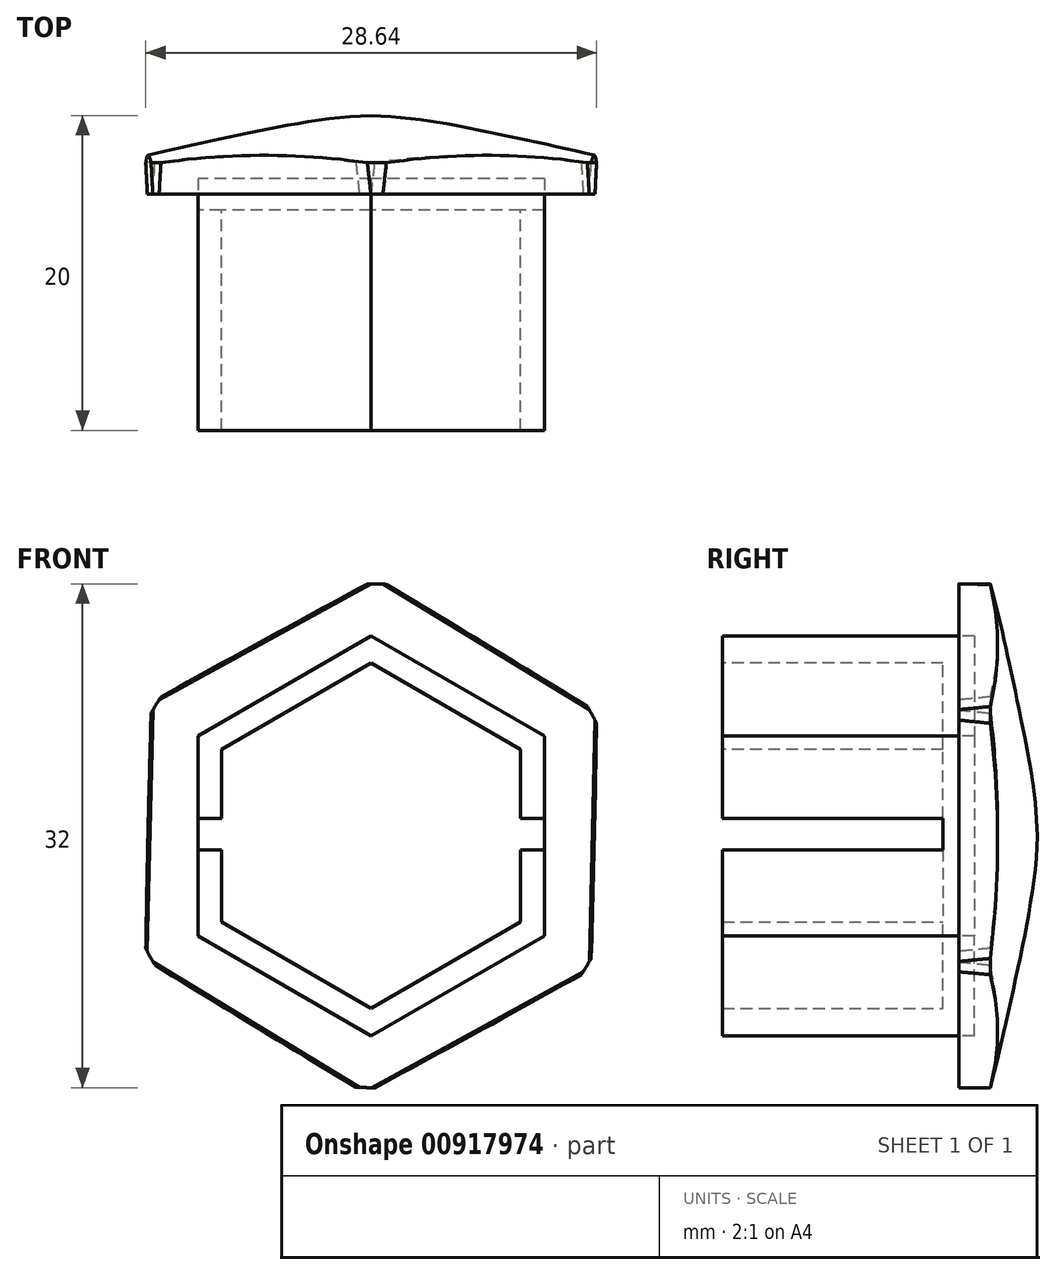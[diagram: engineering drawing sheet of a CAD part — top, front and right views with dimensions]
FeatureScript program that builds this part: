
annotation { "Feature Type Name" : "Feature", "Feature Type Description" : "" }
export const myFeature = defineFeature(function(context is Context, id is Id, definition is map)
    precondition{}
    {
        {
            var Q0;
            Q0=qCreatedBy(makeId("Front.planeOp"),FACE);
            var sketch = newSketch(context, id + "F0", { "sketchPlane" : qUnion([Q0])});
            skCircle(sketch, "E0.cCircle", {"center": v(0, 0) * mm, "radius": 12.7 * mm, "construction": true});
            skLineSegment(sketch, "E0.0", {"start": v(0, -12.7) * mm, "end": v(-11, -6.35) * mm});
            skLineSegment(sketch, "E0.1", {"start": v(-11, -6.35) * mm, "end": v(-11, 6.35) * mm});
            skLineSegment(sketch, "E0.2", {"start": v(-11, 6.35) * mm, "end": v(0, 12.7) * mm});
            skLineSegment(sketch, "E0.3", {"start": v(0, 12.7) * mm, "end": v(11, 6.35) * mm});
            skLineSegment(sketch, "E0.4", {"start": v(11, 6.35) * mm, "end": v(11, -6.35) * mm});
            skLineSegment(sketch, "E0.5", {"start": v(11, -6.35) * mm, "end": v(0, -12.7) * mm});
            skSolve(sketch);
        }
        {
            var Q0;
            Q0=qSketchRegion(id+"F0",true);
            extrude(context, id + "F1", {"entities" : qUnion([Q0]), "depth" : 15 * mm, "offsetDistance" : 25 * mm});
        }
        {
            var Q0;
            Q0=makeQuery(id+"F1.opExtrude","CAP_FACE",FACE,{"disambiguationData":[OSD([sQuery(id+"F0.wireOp",EDGE,"E0.0"),sQuery(id+"F0.wireOp",EDGE,"E0.1"),sQuery(id+"F0.wireOp",EDGE,"E0.2"),sQuery(id+"F0.wireOp",EDGE,"E0.3"),sQuery(id+"F0.wireOp",EDGE,"E0.4"),sQuery(id+"F0.wireOp",EDGE,"E0.5")])],"isStart":false});
            shell(context, id + "F2", {"entities" : qUnion([Q0]), "thickness" : 1.5 * mm});
        }
        {
            var Q0;
            Q0=qCreatedBy(makeId("Top.planeOp"),FACE);
            var sketch = newSketch(context, id + "F3", { "sketchPlane" : qUnion([Q0])});
            skLineSegment(sketch, "E1", {"start": v(0, 0) * mm, "end": v(-16, 0) * mm});
            skLineSegment(sketch, "E2", {"start": v(-16, 0) * mm, "end": v(-16, 2) * mm});
            skFitSpline(sketch, "E3", {"points": [v(-16, 2) * mm, v(-9.06, 3.62) * mm, v(0, 5) * mm], "startDerivative": vector(14.24, 3.9) * mm, "endDerivative": vector(17.69, 0.53) * mm});
            skLineSegment(sketch, "E4", {"start": v(0, 5) * mm, "end": v(0, 0) * mm});
            skSolve(sketch);
        }
        {
            var Q0;
            Q0=makeQuery(id+"F3.imprint","IMPRINT",FACE,{"disambiguationData":[TD([[makeQuery(id+"F3.imprint","IMPRINT",EDGE,{"derivedFrom":sQuery(id+"F3.wireOp",EDGE,"E1")}),-1.0]])]});
            var Q1;
            Q1=sQuery(id+"F3.wireOp",EDGE,"E4");
            revolve(context, id + "F4", {"operationType" : NewBodyOperationType.ADD, "surfaceOperationType" : NewSurfaceOperationType.NEW, "entities" : qUnion([Q0]), "axis" : qUnion([Q1]), "revolveType" : RevolveType.FULL});
        }
        {
            var Q0;
            Q0=qCreatedBy(makeId("Front.planeOp"),FACE);
            var sketch = newSketch(context, id + "F5", { "sketchPlane" : qUnion([Q0])});
            skCircle(sketch, "E5.cCircle", {"center": v(0, 0) * mm, "radius": 16.22 * mm, "construction": true});
            skLineSegment(sketch, "E5.0", {"start": v(13.86, -8.43) * mm, "end": v(-0.37, -16.21) * mm});
            skLineSegment(sketch, "E5.1", {"start": v(-0.37, -16.21) * mm, "end": v(-14.23, -7.79) * mm});
            skLineSegment(sketch, "E5.2", {"start": v(-14.23, -7.79) * mm, "end": v(-13.86, 8.43) * mm});
            skLineSegment(sketch, "E5.3", {"start": v(-13.86, 8.43) * mm, "end": v(0.37, 16.21) * mm});
            skLineSegment(sketch, "E5.4", {"start": v(0.37, 16.21) * mm, "end": v(14.23, 7.79) * mm});
            skLineSegment(sketch, "E5.5", {"start": v(14.23, 7.79) * mm, "end": v(13.86, -8.43) * mm});
            skSolve(sketch);
        }
        {
            var Q0;
            Q0=makeQuery(id+"F5.imprint","IMPRINT",FACE,{"disambiguationData":[TD([[makeQuery(id+"F5.imprint","IMPRINT",EDGE,{"derivedFrom":sQuery(id+"F5.wireOp",EDGE,"E5.0")}),-1.0]])]});
            extrude(context, id + "F6", {"entities" : qUnion([Q0]), "operationType" : NewBodyOperationType.INTERSECT, "oppositeDirection" : true, "depth" : 13.44 * mm, "offsetDistance" : 25 * mm, "hasDraft" : true, "draftAngle" : 3 * degree, "hasSecondDirection" : true, "secondDirectionOppositeDirection" : false, "secondDirectionDepth" : 18.5 * mm});
        }
        {
            var Q0;
            Q0=qCreatedBy(makeId("Front.planeOp"),FACE);
            var sketch = newSketch(context, id + "F7", { "sketchPlane" : qUnion([Q0])});
            skLineSegment(sketch, "E6.bottom", {"start": v(12.11, -0.89) * mm, "end": v(-12.2, -0.89) * mm});
            skLineSegment(sketch, "E6.top", {"start": v(12.11, 1.11) * mm, "end": v(-12.2, 1.11) * mm});
            skLineSegment(sketch, "E6.left", {"start": v(12.11, -0.89) * mm, "end": v(12.11, 1.11) * mm});
            skLineSegment(sketch, "E6.right", {"start": v(-12.2, -0.89) * mm, "end": v(-12.2, 1.11) * mm});
            skSolve(sketch);
        }
        {
            var Q0;
            Q0=makeQuery(id+"F7.imprint","IMPRINT",FACE,{"disambiguationData":[TD([[makeQuery(id+"F7.imprint","IMPRINT",EDGE,{"derivedFrom":sQuery(id+"F7.wireOp",EDGE,"E6.bottom")}),-1.0]])]});
            extrude(context, id + "F8", {"entities" : qUnion([Q0]), "operationType" : NewBodyOperationType.REMOVE, "depth" : 25 * mm, "offsetDistance" : 25 * mm});
        }
        {
            var Q0;
            {var subQ0=sQuery(id+"F0.wireOp",EDGE,"E0.5");var subQ1=sQuery(id+"F0.wireOp",EDGE,"E0.1");var subQ2=sQuery(id+"F0.wireOp",EDGE,"E0.4");var subQ3=sQuery(id+"F0.wireOp",EDGE,"E0.0");Q0=makeQuery(id+"F8.boolean.opBoolean","SPLIT",FACE,{"disambiguationData":[TD([makeQuery(id+"F2.opShell","OFFSET_FACE",FACE,{"disambiguationData":[OSD([subQ3])]})])],"derivedFrom":makeQuery(id+"F2.opShell","OFFSET_FACE",FACE,{"disambiguationData":[OSD([subQ3,subQ1,sQuery(id+"F0.wireOp",EDGE,"E0.2"),sQuery(id+"F0.wireOp",EDGE,"E0.3"),subQ2,subQ0])]})});}
            extrude(context, id + "F9", {"entities" : qUnion([Q0]), "operationType" : NewBodyOperationType.REMOVE, "oppositeDirection" : true, "depth" : 1 * mm, "offsetDistance" : 25 * mm});
        }
        {
            var Q0;
            {var subQ0=sQuery(id+"F0.wireOp",EDGE,"E0.4");var subQ1=sQuery(id+"F0.wireOp",EDGE,"E0.3");var subQ2=sQuery(id+"F0.wireOp",EDGE,"E0.2");var subQ3=sQuery(id+"F0.wireOp",EDGE,"E0.1");Q0=makeQuery(id+"F8.boolean.opBoolean","SPLIT",FACE,{"disambiguationData":[TD([makeQuery(id+"F2.opShell","OFFSET_FACE",FACE,{"disambiguationData":[OSD([subQ2])]})])],"derivedFrom":makeQuery(id+"F2.opShell","OFFSET_FACE",FACE,{"disambiguationData":[OSD([sQuery(id+"F0.wireOp",EDGE,"E0.0"),subQ3,subQ2,subQ1,subQ0,sQuery(id+"F0.wireOp",EDGE,"E0.5")])]})});}
            var Q1;
            Q1=makeQuery(id+"F0.imprint","IMPRINT",FACE,{"disambiguationData":[TD([[makeQuery(id+"F0.imprint","IMPRINT",EDGE,{"derivedFrom":sQuery(id+"F0.wireOp",EDGE,"E0.0")}),-1.0]])]});
            extrude(context, id + "F10", {"entities" : qUnion([Q0, Q1]), "operationType" : NewBodyOperationType.REMOVE, "oppositeDirection" : true, "depth" : 1 * mm, "offsetDistance" : 25 * mm});
        }
        {
            var Q0;
            Q0=makeQuery(id+"F0.imprint","IMPRINT",FACE,{"disambiguationData":[TD([[makeQuery(id+"F0.imprint","IMPRINT",EDGE,{"derivedFrom":sQuery(id+"F0.wireOp",EDGE,"E0.0")}),-1.0]])]});
            extrude(context, id + "F11", {"entities" : qUnion([Q0]), "operationType" : NewBodyOperationType.ADD, "depth" : 1 * mm, "offsetDistance" : 25 * mm});
        }
    });
